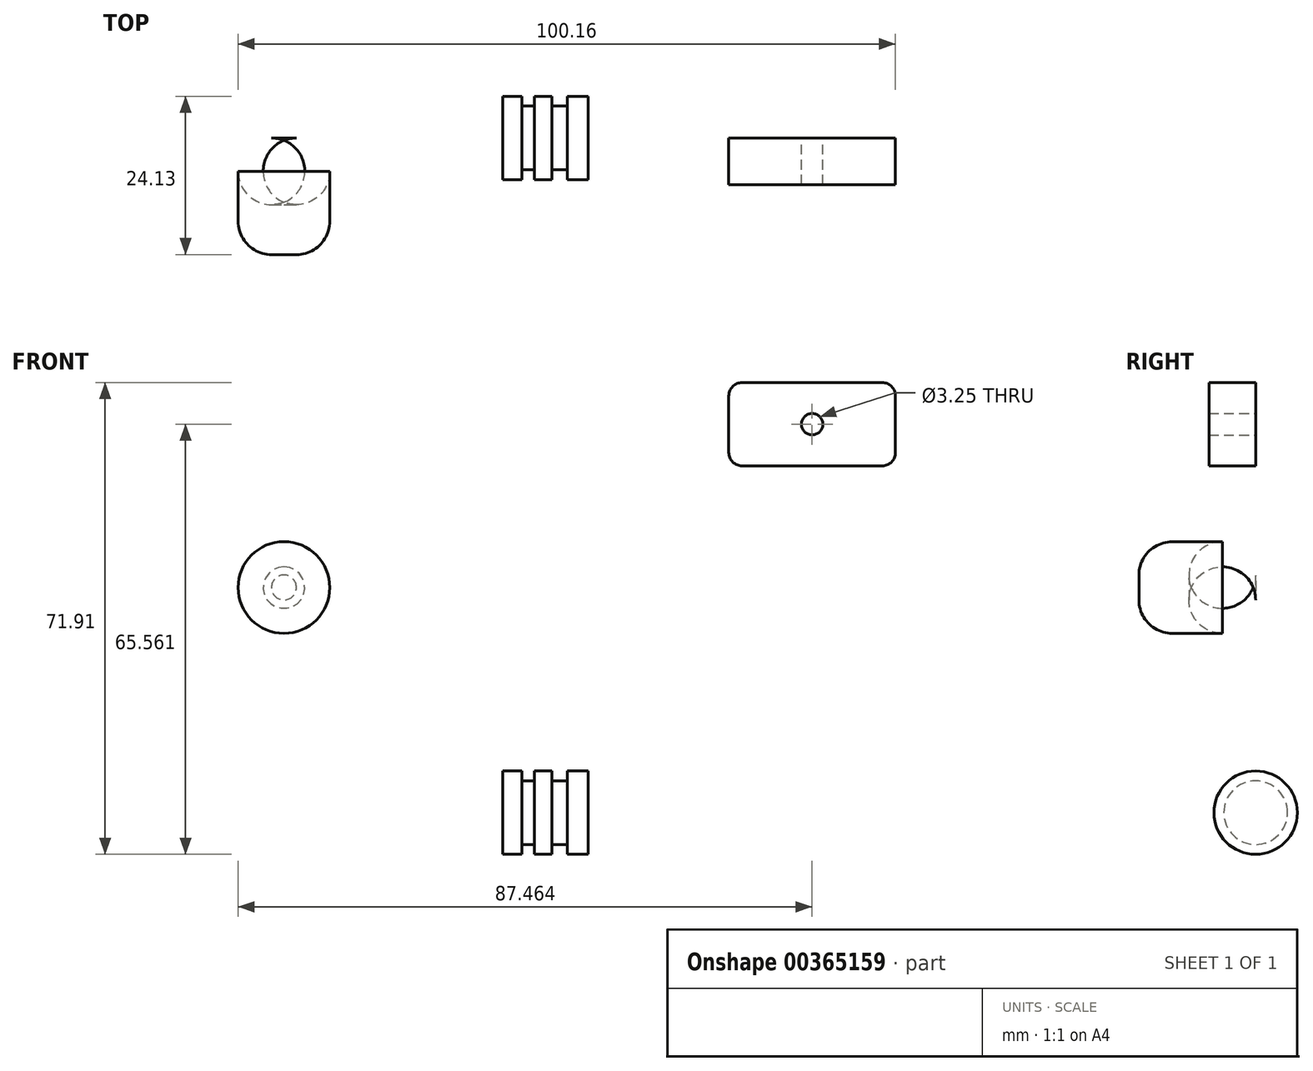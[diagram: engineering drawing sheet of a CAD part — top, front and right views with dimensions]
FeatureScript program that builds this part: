
annotation { "Feature Type Name" : "Feature", "Feature Type Description" : "" }
export const myFeature = defineFeature(function(context is Context, id is Id, definition is map)
    precondition{}
    {
        {
            var Q0;
            Q0=qCreatedBy(makeId("Front.planeOp"),FACE);
            var sketch = newSketch(context, id + "F0", { "sketchPlane" : qUnion([Q0])});
            skLineSegment(sketch, "E0", {"start": v(-8.86, 0) * mm, "end": v(-8.86, 6.35) * mm});
            skLineSegment(sketch, "E1", {"start": v(-8.86, 6.35) * mm, "end": v(-5.95, 6.35) * mm});
            skLineSegment(sketch, "E2", {"start": v(-5.95, 6.35) * mm, "end": v(-5.95, 4.86) * mm});
            skLineSegment(sketch, "E3", {"start": v(-5.95, 4.86) * mm, "end": v(-4.06, 4.86) * mm});
            skLineSegment(sketch, "E4", {"start": v(-4.06, 4.86) * mm, "end": v(-4.06, 6.35) * mm});
            skLineSegment(sketch, "E5", {"start": v(-4.06, 6.35) * mm, "end": v(-1.4, 6.35) * mm});
            skLineSegment(sketch, "E6", {"start": v(-1.4, 6.35) * mm, "end": v(-1.4, 4.86) * mm});
            skLineSegment(sketch, "E7", {"start": v(-1.4, 4.86) * mm, "end": v(0.96, 4.86) * mm});
            skLineSegment(sketch, "E8", {"start": v(0.96, 4.86) * mm, "end": v(0.96, 6.35) * mm});
            skPoint(sketch, "E8.endSnap0", {"position": v(-2.73, 6.35) * mm});
            skLineSegment(sketch, "E9", {"start": v(0.96, 6.35) * mm, "end": v(4.1, 6.35) * mm});
            skLineSegment(sketch, "E10", {"start": v(4.1, 6.35) * mm, "end": v(4.1, 0) * mm});
            skLineSegment(sketch, "E11", {"start": v(4.1, 0) * mm, "end": v(-8.86, 0) * mm});
            skSolve(sketch);
        }
        {
            var Q0;
            Q0=makeQuery(id+"F0.imprint","IMPRINT",FACE,{"disambiguationData":[TD([[makeQuery(id+"F0.imprint","IMPRINT",EDGE,{"derivedFrom":sQuery(id+"F0.wireOp",EDGE,"E0")}),-1.0]])]});
            var Q1;
            Q1=sQuery(id+"F0.wireOp",EDGE,"E11");
            revolve(context, id + "F1", {"entities" : qUnion([Q0]), "axis" : qUnion([Q1]), "revolveType" : RevolveType.FULL});
        }
        {
            var Q0;
            Q0=qCreatedBy(makeId("Front.planeOp"),FACE);
            var sketch = newSketch(context, id + "F2", { "sketchPlane" : qUnion([Q0])});
            skCircle(sketch, "E12", {"center": v(-42.21, 34.32) * mm, "radius": 6.99 * mm});
            skSolve(sketch);
        }
        {
            var Q0;
            Q0=makeQuery(id+"F2.imprint","IMPRINT",FACE,{"disambiguationData":[TD([[makeQuery(id+"F2.imprint","IMPRINT",EDGE,{"derivedFrom":sQuery(id+"F2.wireOp",EDGE,"E12")}),1.0]])]});
            extrude(context, id + "F3", {"entities" : qUnion([Q0]), "depth" : 17.78 * mm});
        }
        {
            var Q0;
            Q0=makeQuery(id+"F3.opExtrude","CAP_FACE",FACE,{"disambiguationData":[OSD([sQuery(id+"F2.wireOp",EDGE,"E12")])],"isStart":false});
            var Q1;
            Q1=makeQuery(id+"F3.opExtrude","CAP_FACE",FACE,{"disambiguationData":[OSD([sQuery(id+"F2.wireOp",EDGE,"E12")])],"isStart":true});
            fillet(context, id + "F4", {"entities" : qUnion([Q0, Q1]), "radius" : 5.08 * mm, "tangentPropagation" : true, "allowEdgeOverflow" : false});
        }
        {
            var Q0;
            Q0=qCreatedBy(makeId("Front.planeOp"),FACE);
            var sketch = newSketch(context, id + "F5", { "sketchPlane" : qUnion([Q0])});
            skLineSegment(sketch, "E13.bottom", {"start": v(25.56, 65.56) * mm, "end": v(50.96, 65.56) * mm});
            skLineSegment(sketch, "E13.top", {"start": v(25.56, 52.86) * mm, "end": v(50.96, 52.86) * mm});
            skLineSegment(sketch, "E13.left", {"start": v(25.56, 65.56) * mm, "end": v(25.56, 52.86) * mm});
            skLineSegment(sketch, "E13.right", {"start": v(50.96, 65.56) * mm, "end": v(50.96, 52.86) * mm});
            skCircle(sketch, "E14", {"center": v(38.26, 59.21) * mm, "radius": 1.63 * mm});
            skPoint(sketch, "E14.centerSnap0", {"position": v(25.56, 59.21) * mm});
            skPoint(sketch, "E14.centerSnap1", {"position": v(38.26, 65.56) * mm});
            skSolve(sketch);
        }
        {
            var Q0;
            Q0=makeQuery(id+"F5.imprint","IMPRINT",FACE,{"disambiguationData":[TD([[makeQuery(id+"F5.imprint","IMPRINT",EDGE,{"derivedFrom":sQuery(id+"F5.wireOp",EDGE,"E13.bottom")}),-1.0]])]});
            extrude(context, id + "F6", {"entities" : qUnion([Q0]), "depth" : 7.11 * mm});
        }
        {
            var Q0;
            Q0=makeQuery(id+"F6.opExtrude","SWEPT_EDGE",EDGE,{"disambiguationData":[OSD([sQuery(id+"F5.wireOp",EDGE,"E13.bottom"),sQuery(id+"F5.wireOp",EDGE,"E13.right")])]});
            var Q1;
            Q1=makeQuery(id+"F6.opExtrude","SWEPT_EDGE",EDGE,{"disambiguationData":[OSD([sQuery(id+"F5.wireOp",EDGE,"E13.bottom"),sQuery(id+"F5.wireOp",EDGE,"E13.left")])]});
            var Q2;
            Q2=makeQuery(id+"F6.opExtrude","SWEPT_EDGE",EDGE,{"disambiguationData":[OSD([sQuery(id+"F5.wireOp",EDGE,"E13.top"),sQuery(id+"F5.wireOp",EDGE,"E13.left")])]});
            var Q3;
            Q3=makeQuery(id+"F6.opExtrude","SWEPT_EDGE",EDGE,{"disambiguationData":[OSD([sQuery(id+"F5.wireOp",EDGE,"E13.top"),sQuery(id+"F5.wireOp",EDGE,"E13.right")])]});
            fillet(context, id + "F7", {"entities" : qUnion([Q0, Q1, Q2, Q3]), "radius" : 2.03 * mm, "tangentPropagation" : true, "allowEdgeOverflow" : false});
        }
    });
